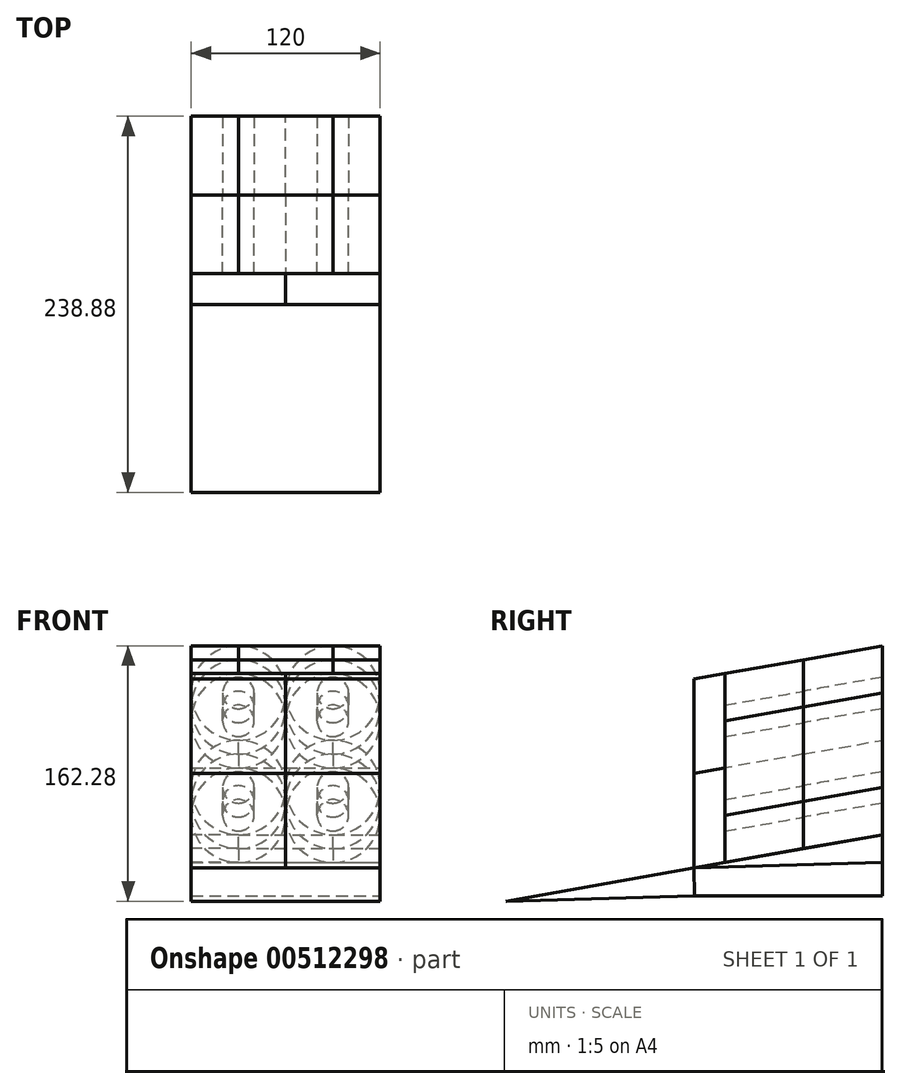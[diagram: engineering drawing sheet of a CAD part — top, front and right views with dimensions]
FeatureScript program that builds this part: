
annotation { "Feature Type Name" : "Feature", "Feature Type Description" : "" }
export const myFeature = defineFeature(function(context is Context, id is Id, definition is map)
    precondition{}
    {
        {
            var Q0;
            Q0=qCreatedBy(makeId("Front.planeOp"),FACE);
            var sketch = newSketch(context, id + "F0", { "sketchPlane" : qUnion([Q0])});
            skLineSegment(sketch, "E0", {"start": v(0, 0) * mm, "end": v(-30, 0) * mm});
            skLineSegment(sketch, "E1", {"start": v(-30, 0) * mm, "end": v(0, 0) * mm});
            skLineSegment(sketch, "E2", {"start": v(0, 0) * mm, "end": v(30, 0) * mm});
            skCircle(sketch, "E3", {"center": v(-30, 0) * mm, "radius": 30 * mm});
            skCircle(sketch, "E4", {"center": v(30, 0) * mm, "radius": 30 * mm});
            skLineSegment(sketch, "E5", {"start": v(30, 0) * mm, "end": v(40, 0) * mm});
            skLineSegment(sketch, "E6", {"start": v(-30, 0) * mm, "end": v(-40, 0) * mm});
            skCircle(sketch, "E7", {"center": v(-30, 0) * mm, "radius": 10 * mm});
            skCircle(sketch, "E8", {"center": v(30, 0) * mm, "radius": 10 * mm});
            skLineSegment(sketch, "E9", {"start": v(-30, 0) * mm, "end": v(-30, 60) * mm});
            skLineSegment(sketch, "E10", {"start": v(30, 0) * mm, "end": v(30, 60) * mm});
            skCircle(sketch, "E11", {"center": v(-30, 60) * mm, "radius": 30 * mm});
            skCircle(sketch, "E12", {"center": v(30, 60) * mm, "radius": 30 * mm});
            skLineSegment(sketch, "E13", {"start": v(-30, 60) * mm, "end": v(-20, 60) * mm});
            skLineSegment(sketch, "E14", {"start": v(30, 60) * mm, "end": v(20, 60) * mm});
            skCircle(sketch, "E15", {"center": v(-30, 60) * mm, "radius": 10 * mm});
            skCircle(sketch, "E16", {"center": v(30, 60) * mm, "radius": 10 * mm});
            skPoint(sketch, "E17", {"position": v(0, 30) * mm});
            skLineSegment(sketch, "E18.bottom", {"start": v(0, 30) * mm, "end": v(-60, 30) * mm});
            skLineSegment(sketch, "E18.top", {"start": v(0, -30) * mm, "end": v(-60, -30) * mm});
            skLineSegment(sketch, "E18.left", {"start": v(0, 30) * mm, "end": v(0, -30) * mm});
            skLineSegment(sketch, "E18.right", {"start": v(-60, 30) * mm, "end": v(-60, -30) * mm});
            skLineSegment(sketch, "E19.top", {"start": v(0, 90) * mm, "end": v(-60, 90) * mm});
            skLineSegment(sketch, "E19.left", {"start": v(0, 30) * mm, "end": v(0, 90) * mm});
            skLineSegment(sketch, "E19.right", {"start": v(-60, 30) * mm, "end": v(-60, 90) * mm});
            skLineSegment(sketch, "E20.bottom", {"start": v(0, -30) * mm, "end": v(60, -30) * mm});
            skLineSegment(sketch, "E20.top", {"start": v(0, 30) * mm, "end": v(60, 30) * mm});
            skLineSegment(sketch, "E20.left", {"start": v(0, -30) * mm, "end": v(0, 30) * mm});
            skLineSegment(sketch, "E20.right", {"start": v(60, -30) * mm, "end": v(60, 30) * mm});
            skLineSegment(sketch, "E21.top", {"start": v(0, 90) * mm, "end": v(60, 90) * mm});
            skLineSegment(sketch, "E21.right", {"start": v(60, 30) * mm, "end": v(60, 90) * mm});
            skSolve(sketch);
        }
        {
            var Q0;
            Q0=qCreatedBy(makeId("Front.planeOp"),FACE);
            var sketch = newSketch(context, id + "F1", { "sketchPlane" : qUnion([Q0])});
            skPoint(sketch, "E22", {"position": v(-30, 60) * mm});
            skPoint(sketch, "E23", {"position": v(30, 60) * mm});
            skPoint(sketch, "E24", {"position": v(-30, 0) * mm});
            skPoint(sketch, "E25", {"position": v(30, 0) * mm});
            skCircle(sketch, "E26", {"center": v(-30, 60) * mm, "radius": 10 * mm});
            skCircle(sketch, "E27", {"center": v(30, 60) * mm, "radius": 10 * mm});
            skCircle(sketch, "E28", {"center": v(30, 0) * mm, "radius": 10 * mm});
            skCircle(sketch, "E29", {"center": v(-30, 0) * mm, "radius": 10 * mm});
            skSolve(sketch);
        }
        {
            var Q0;
            Q0=qCreatedBy(makeId("Right.planeOp"),FACE);
            var sketch = newSketch(context, id + "F2", { "sketchPlane" : qUnion([Q0])});
            skLineSegment(sketch, "E30", {"start": v(0, -30) * mm, "end": v(50, -30) * mm});
            skLineSegment(sketch, "E31", {"start": v(0, -30) * mm, "end": v(0, -38.83) * mm});
            skLineSegment(sketch, "E32", {"start": v(0, -38.83) * mm, "end": v(0, -30) * mm});
            skLineSegment(sketch, "E33", {"start": v(50, -30) * mm, "end": v(50, -21.17) * mm});
            skLineSegment(sketch, "E34", {"start": v(0, -38.83) * mm, "end": v(-50, -38.83) * mm});
            skLineSegment(sketch, "E35", {"start": v(-50, -38.83) * mm, "end": v(0, -30) * mm});
            skLineSegment(sketch, "E36", {"start": v(50, -21.17) * mm, "end": v(0, -30) * mm});
            skSolve(sketch);
        }
        {
            var Q0;
            Q0 = qSketchRegion(id + "F1", true);
            var Q1;
            Q1=sQuery(id+"F2.wireOp",EDGE,"E35");
            var Q2;
            Q2=sQuery(id+"F2.wireOp",EDGE,"my1mdeSe-ST6u-0EiF-3ExV-mTvrdPK5u88H");
            sweep(context, id + "F3", {"profiles" : qUnion([Q0]), "path" : qUnion([Q1, Q2])});
        }
        {
            var Q0;
            Q0 = qSketchRegion(id + "F1", true);
            var Q1;
            Q1=sQuery(id+"F2.wireOp",EDGE,"E36");
            sweep(context, id + "F4", {"profiles" : qUnion([Q0]), "path" : qUnion([Q1])});
        }
        {
            var Q0;
            {var subQ3=sQuery(id+"F0.wireOp",EDGE,"E11");var subQ5=sQuery(id+"F0.wireOp",EDGE,"E12");var subQ6=makeQuery(id+"F0.imprint","INTERSECT",VERTEX,{"derivedFrom":[subQ3,subQ5]});Q0=makeQuery(id+"F0.imprint","IMPRINT",FACE,{"disambiguationData":[TD([[makeQuery(id+"F0.imprint","IMPRINT",EDGE,{"disambiguationData":[TD([[subQ6,1.0]])],"derivedFrom":subQ3}),-1.0]])]});}
            var Q1;
            {var subQ0=sQuery(id+"F0.wireOp",EDGE,"E20.left");var subQ3=sQuery(id+"F0.wireOp",EDGE,"E18.bottom");var subQ5=makeQuery(id+"F0.imprint","INTERSECT",VERTEX,{"derivedFrom":[subQ3,subQ0,sQuery(id+"F0.wireOp",EDGE,"E20.top"),sQuery(id+"F0.wireOp",EDGE,"E19.left")]});Q1=makeQuery(id+"F0.imprint","IMPRINT",FACE,{"disambiguationData":[TD([[makeQuery(id+"F0.imprint","IMPRINT",EDGE,{"disambiguationData":[TD([[subQ5,-1.0]])],"derivedFrom":subQ3}),1.0]])]});}
            var Q2;
            {var subQ0=sQuery(id+"F0.wireOp",EDGE,"E20.left");var subQ3=sQuery(id+"F0.wireOp",EDGE,"E20.top");var subQ5=makeQuery(id+"F0.imprint","INTERSECT",VERTEX,{"derivedFrom":[sQuery(id+"F0.wireOp",EDGE,"E18.bottom"),subQ0,subQ3,sQuery(id+"F0.wireOp",EDGE,"E19.left")]});Q2=makeQuery(id+"F0.imprint","IMPRINT",FACE,{"disambiguationData":[TD([[makeQuery(id+"F0.imprint","IMPRINT",EDGE,{"disambiguationData":[TD([[subQ5,-1.0]])],"derivedFrom":subQ3}),-1.0]])]});}
            var Q3;
            {var subQ0=sQuery(id+"F0.wireOp",EDGE,"E19.left");var subQ1=sQuery(id+"F0.wireOp",EDGE,"E12");var subQ2=makeQuery(id+"F0.imprint","INTERSECT",VERTEX,{"derivedFrom":[sQuery(id+"F0.wireOp",EDGE,"E11"),subQ1,subQ0]});Q3=makeQuery(id+"F0.imprint","IMPRINT",FACE,{"disambiguationData":[TD([[makeQuery(id+"F0.imprint","IMPRINT",EDGE,{"disambiguationData":[TD([[subQ2,-1.0]])],"derivedFrom":subQ1}),-1.0]])]});}
            var Q4;
            {var subQ0=sQuery(id+"F0.wireOp",EDGE,"E21.right");var subQ1=sQuery(id+"F0.wireOp",EDGE,"E12");var subQ2=makeQuery(id+"F0.imprint","INTERSECT",VERTEX,{"derivedFrom":[subQ1,subQ0]});Q4=makeQuery(id+"F0.imprint","IMPRINT",FACE,{"disambiguationData":[TD([[makeQuery(id+"F0.imprint","IMPRINT",EDGE,{"disambiguationData":[TD([[subQ2,1.0]])],"derivedFrom":subQ0}),1.0]])]});}
            var Q5;
            {var subQ0=sQuery(id+"F0.wireOp",EDGE,"E20.right");var subQ1=sQuery(id+"F0.wireOp",EDGE,"E4");var subQ2=makeQuery(id+"F0.imprint","INTERSECT",VERTEX,{"derivedFrom":[subQ1,subQ0]});Q5=makeQuery(id+"F0.imprint","IMPRINT",FACE,{"disambiguationData":[TD([[makeQuery(id+"F0.imprint","IMPRINT",EDGE,{"disambiguationData":[TD([[subQ2,-1.0]])],"derivedFrom":subQ0}),1.0]])]});}
            var Q6;
            {var subQ0=sQuery(id+"F0.wireOp",EDGE,"E20.right");var subQ1=sQuery(id+"F0.wireOp",EDGE,"E4");var subQ2=makeQuery(id+"F0.imprint","INTERSECT",VERTEX,{"derivedFrom":[subQ1,subQ0]});Q6=makeQuery(id+"F0.imprint","IMPRINT",FACE,{"disambiguationData":[TD([[makeQuery(id+"F0.imprint","IMPRINT",EDGE,{"disambiguationData":[TD([[subQ2,1.0]])],"derivedFrom":subQ1}),-1.0]])]});}
            var Q7;
            {var subQ1=sQuery(id+"F0.wireOp",EDGE,"E4");var subQ3=sQuery(id+"F0.wireOp",EDGE,"E20.bottom");var subQ4=makeQuery(id+"F0.imprint","INTERSECT",VERTEX,{"derivedFrom":[subQ1,subQ3]});Q7=makeQuery(id+"F0.imprint","IMPRINT",FACE,{"disambiguationData":[TD([[makeQuery(id+"F0.imprint","IMPRINT",EDGE,{"disambiguationData":[TD([[subQ4,1.0]])],"derivedFrom":subQ3}),1.0]])]});}
            var Q8;
            {var subQ1=sQuery(id+"F0.wireOp",EDGE,"E3");var subQ3=sQuery(id+"F0.wireOp",EDGE,"E18.top");var subQ4=makeQuery(id+"F0.imprint","INTERSECT",VERTEX,{"derivedFrom":[subQ1,subQ3]});Q8=makeQuery(id+"F0.imprint","IMPRINT",FACE,{"disambiguationData":[TD([[makeQuery(id+"F0.imprint","IMPRINT",EDGE,{"disambiguationData":[TD([[subQ4,1.0]])],"derivedFrom":subQ3}),-1.0]])]});}
            var Q9;
            {var subQ0=sQuery(id+"F0.wireOp",EDGE,"E18.right");var subQ1=sQuery(id+"F0.wireOp",EDGE,"E3");var subQ2=makeQuery(id+"F0.imprint","INTERSECT",VERTEX,{"derivedFrom":[subQ1,subQ0]});Q9=makeQuery(id+"F0.imprint","IMPRINT",FACE,{"disambiguationData":[TD([[makeQuery(id+"F0.imprint","IMPRINT",EDGE,{"disambiguationData":[TD([[subQ2,-1.0]])],"derivedFrom":subQ1}),-1.0]])]});}
            var Q10;
            {var subQ0=sQuery(id+"F0.wireOp",EDGE,"E18.right");var subQ1=sQuery(id+"F0.wireOp",EDGE,"E3");var subQ2=makeQuery(id+"F0.imprint","INTERSECT",VERTEX,{"derivedFrom":[subQ1,subQ0]});Q10=makeQuery(id+"F0.imprint","IMPRINT",FACE,{"disambiguationData":[TD([[makeQuery(id+"F0.imprint","IMPRINT",EDGE,{"disambiguationData":[TD([[subQ2,1.0]])],"derivedFrom":subQ0}),1.0]])]});}
            var Q11;
            {var subQ0=sQuery(id+"F0.wireOp",EDGE,"E19.right");var subQ1=sQuery(id+"F0.wireOp",EDGE,"E11");var subQ2=makeQuery(id+"F0.imprint","INTERSECT",VERTEX,{"derivedFrom":[subQ1,subQ0]});Q11=makeQuery(id+"F0.imprint","IMPRINT",FACE,{"disambiguationData":[TD([[makeQuery(id+"F0.imprint","IMPRINT",EDGE,{"disambiguationData":[TD([[subQ2,1.0]])],"derivedFrom":subQ0}),-1.0]])]});}
            var Q12;
            {var subQ0=sQuery(id+"F0.wireOp",EDGE,"E19.top");var subQ1=sQuery(id+"F0.wireOp",EDGE,"E11");var subQ2=makeQuery(id+"F0.imprint","INTERSECT",VERTEX,{"derivedFrom":[subQ1,subQ0]});Q12=makeQuery(id+"F0.imprint","IMPRINT",FACE,{"disambiguationData":[TD([[makeQuery(id+"F0.imprint","IMPRINT",EDGE,{"disambiguationData":[TD([[subQ2,-1.0]])],"derivedFrom":subQ1}),-1.0]])]});}
            var Q13;
            {var subQ0=sQuery(id+"F0.wireOp",EDGE,"E19.top");var subQ1=sQuery(id+"F0.wireOp",EDGE,"E11");var subQ2=makeQuery(id+"F0.imprint","INTERSECT",VERTEX,{"derivedFrom":[subQ1,subQ0]});Q13=makeQuery(id+"F0.imprint","IMPRINT",FACE,{"disambiguationData":[TD([[makeQuery(id+"F0.imprint","IMPRINT",EDGE,{"disambiguationData":[TD([[subQ2,1.0]])],"derivedFrom":subQ1}),-1.0]])]});}
            var Q14;
            {var subQ0=sQuery(id+"F0.wireOp",EDGE,"E21.top");var subQ1=sQuery(id+"F0.wireOp",EDGE,"E12");var subQ2=makeQuery(id+"F0.imprint","INTERSECT",VERTEX,{"derivedFrom":[subQ1,subQ0]});Q14=makeQuery(id+"F0.imprint","IMPRINT",FACE,{"disambiguationData":[TD([[makeQuery(id+"F0.imprint","IMPRINT",EDGE,{"disambiguationData":[TD([[subQ2,-1.0]])],"derivedFrom":subQ1}),-1.0]])]});}
            var Q15;
            {var subQ0=sQuery(id+"F0.wireOp",EDGE,"E21.top");var subQ1=sQuery(id+"F0.wireOp",EDGE,"E12");var subQ2=makeQuery(id+"F0.imprint","INTERSECT",VERTEX,{"derivedFrom":[subQ1,subQ0]});Q15=makeQuery(id+"F0.imprint","IMPRINT",FACE,{"disambiguationData":[TD([[makeQuery(id+"F0.imprint","IMPRINT",EDGE,{"disambiguationData":[TD([[subQ2,1.0]])],"derivedFrom":subQ1}),-1.0]])]});}
            var Q16;
            Q16=sQuery(id+"F2.wireOp",EDGE,"E36");
            sweep(context, id + "F5", {"profiles" : qUnion([Q0, Q1, Q2, Q3, Q4, Q5, Q6, Q7, Q8, Q9, Q10, Q11, Q12, Q13, Q14, Q15]), "path" : qUnion([Q16])});
        }
        {
            var Q0;
            {var subQ3=sQuery(id+"F0.wireOp",EDGE,"E11");var subQ5=sQuery(id+"F0.wireOp",EDGE,"E12");var subQ6=makeQuery(id+"F0.imprint","INTERSECT",VERTEX,{"derivedFrom":[subQ3,subQ5]});Q0=makeQuery(id+"F0.imprint","IMPRINT",FACE,{"disambiguationData":[TD([[makeQuery(id+"F0.imprint","IMPRINT",EDGE,{"disambiguationData":[TD([[subQ6,1.0]])],"derivedFrom":subQ3}),-1.0]])]});}
            var Q1;
            {var subQ0=sQuery(id+"F0.wireOp",EDGE,"E19.left");var subQ1=sQuery(id+"F0.wireOp",EDGE,"E12");var subQ2=makeQuery(id+"F0.imprint","INTERSECT",VERTEX,{"derivedFrom":[sQuery(id+"F0.wireOp",EDGE,"E11"),subQ1,subQ0]});Q1=makeQuery(id+"F0.imprint","IMPRINT",FACE,{"disambiguationData":[TD([[makeQuery(id+"F0.imprint","IMPRINT",EDGE,{"disambiguationData":[TD([[subQ2,-1.0]])],"derivedFrom":subQ1}),-1.0]])]});}
            var Q2;
            {var subQ0=sQuery(id+"F0.wireOp",EDGE,"E20.left");var subQ3=sQuery(id+"F0.wireOp",EDGE,"E20.top");var subQ5=makeQuery(id+"F0.imprint","INTERSECT",VERTEX,{"derivedFrom":[sQuery(id+"F0.wireOp",EDGE,"E18.bottom"),subQ0,subQ3,sQuery(id+"F0.wireOp",EDGE,"E19.left")]});Q2=makeQuery(id+"F0.imprint","IMPRINT",FACE,{"disambiguationData":[TD([[makeQuery(id+"F0.imprint","IMPRINT",EDGE,{"disambiguationData":[TD([[subQ5,-1.0]])],"derivedFrom":subQ3}),-1.0]])]});}
            var Q3;
            {var subQ0=sQuery(id+"F0.wireOp",EDGE,"E20.left");var subQ3=sQuery(id+"F0.wireOp",EDGE,"E18.bottom");var subQ5=makeQuery(id+"F0.imprint","INTERSECT",VERTEX,{"derivedFrom":[subQ3,subQ0,sQuery(id+"F0.wireOp",EDGE,"E20.top"),sQuery(id+"F0.wireOp",EDGE,"E19.left")]});Q3=makeQuery(id+"F0.imprint","IMPRINT",FACE,{"disambiguationData":[TD([[makeQuery(id+"F0.imprint","IMPRINT",EDGE,{"disambiguationData":[TD([[subQ5,-1.0]])],"derivedFrom":subQ3}),1.0]])]});}
            var Q4;
            {var subQ0=sQuery(id+"F0.wireOp",EDGE,"E21.top");var subQ1=sQuery(id+"F0.wireOp",EDGE,"E12");var subQ2=makeQuery(id+"F0.imprint","INTERSECT",VERTEX,{"derivedFrom":[subQ1,subQ0]});Q4=makeQuery(id+"F0.imprint","IMPRINT",FACE,{"disambiguationData":[TD([[makeQuery(id+"F0.imprint","IMPRINT",EDGE,{"disambiguationData":[TD([[subQ2,-1.0]])],"derivedFrom":subQ1}),-1.0]])]});}
            var Q5;
            {var subQ0=sQuery(id+"F0.wireOp",EDGE,"E19.top");var subQ1=sQuery(id+"F0.wireOp",EDGE,"E11");var subQ2=makeQuery(id+"F0.imprint","INTERSECT",VERTEX,{"derivedFrom":[subQ1,subQ0]});Q5=makeQuery(id+"F0.imprint","IMPRINT",FACE,{"disambiguationData":[TD([[makeQuery(id+"F0.imprint","IMPRINT",EDGE,{"disambiguationData":[TD([[subQ2,1.0]])],"derivedFrom":subQ1}),-1.0]])]});}
            var Q6;
            {var subQ0=sQuery(id+"F0.wireOp",EDGE,"E21.top");var subQ1=sQuery(id+"F0.wireOp",EDGE,"E12");var subQ2=makeQuery(id+"F0.imprint","INTERSECT",VERTEX,{"derivedFrom":[subQ1,subQ0]});Q6=makeQuery(id+"F0.imprint","IMPRINT",FACE,{"disambiguationData":[TD([[makeQuery(id+"F0.imprint","IMPRINT",EDGE,{"disambiguationData":[TD([[subQ2,1.0]])],"derivedFrom":subQ1}),-1.0]])]});}
            var Q7;
            {var subQ0=sQuery(id+"F0.wireOp",EDGE,"E21.right");var subQ1=sQuery(id+"F0.wireOp",EDGE,"E12");var subQ2=makeQuery(id+"F0.imprint","INTERSECT",VERTEX,{"derivedFrom":[subQ1,subQ0]});Q7=makeQuery(id+"F0.imprint","IMPRINT",FACE,{"disambiguationData":[TD([[makeQuery(id+"F0.imprint","IMPRINT",EDGE,{"disambiguationData":[TD([[subQ2,1.0]])],"derivedFrom":subQ0}),1.0]])]});}
            var Q8;
            {var subQ0=sQuery(id+"F0.wireOp",EDGE,"E20.right");var subQ1=sQuery(id+"F0.wireOp",EDGE,"E4");var subQ2=makeQuery(id+"F0.imprint","INTERSECT",VERTEX,{"derivedFrom":[subQ1,subQ0]});Q8=makeQuery(id+"F0.imprint","IMPRINT",FACE,{"disambiguationData":[TD([[makeQuery(id+"F0.imprint","IMPRINT",EDGE,{"disambiguationData":[TD([[subQ2,-1.0]])],"derivedFrom":subQ0}),1.0]])]});}
            var Q9;
            {var subQ0=sQuery(id+"F0.wireOp",EDGE,"E20.right");var subQ1=sQuery(id+"F0.wireOp",EDGE,"E4");var subQ2=makeQuery(id+"F0.imprint","INTERSECT",VERTEX,{"derivedFrom":[subQ1,subQ0]});Q9=makeQuery(id+"F0.imprint","IMPRINT",FACE,{"disambiguationData":[TD([[makeQuery(id+"F0.imprint","IMPRINT",EDGE,{"disambiguationData":[TD([[subQ2,1.0]])],"derivedFrom":subQ1}),-1.0]])]});}
            var Q10;
            {var subQ1=sQuery(id+"F0.wireOp",EDGE,"E4");var subQ3=sQuery(id+"F0.wireOp",EDGE,"E20.bottom");var subQ4=makeQuery(id+"F0.imprint","INTERSECT",VERTEX,{"derivedFrom":[subQ1,subQ3]});Q10=makeQuery(id+"F0.imprint","IMPRINT",FACE,{"disambiguationData":[TD([[makeQuery(id+"F0.imprint","IMPRINT",EDGE,{"disambiguationData":[TD([[subQ4,1.0]])],"derivedFrom":subQ3}),1.0]])]});}
            var Q11;
            {var subQ1=sQuery(id+"F0.wireOp",EDGE,"E3");var subQ3=sQuery(id+"F0.wireOp",EDGE,"E18.top");var subQ4=makeQuery(id+"F0.imprint","INTERSECT",VERTEX,{"derivedFrom":[subQ1,subQ3]});Q11=makeQuery(id+"F0.imprint","IMPRINT",FACE,{"disambiguationData":[TD([[makeQuery(id+"F0.imprint","IMPRINT",EDGE,{"disambiguationData":[TD([[subQ4,1.0]])],"derivedFrom":subQ3}),-1.0]])]});}
            var Q12;
            {var subQ0=sQuery(id+"F0.wireOp",EDGE,"E18.right");var subQ1=sQuery(id+"F0.wireOp",EDGE,"E3");var subQ2=makeQuery(id+"F0.imprint","INTERSECT",VERTEX,{"derivedFrom":[subQ1,subQ0]});Q12=makeQuery(id+"F0.imprint","IMPRINT",FACE,{"disambiguationData":[TD([[makeQuery(id+"F0.imprint","IMPRINT",EDGE,{"disambiguationData":[TD([[subQ2,1.0]])],"derivedFrom":subQ0}),1.0]])]});}
            var Q13;
            {var subQ0=sQuery(id+"F0.wireOp",EDGE,"E19.right");var subQ1=sQuery(id+"F0.wireOp",EDGE,"E11");var subQ2=makeQuery(id+"F0.imprint","INTERSECT",VERTEX,{"derivedFrom":[subQ1,subQ0]});Q13=makeQuery(id+"F0.imprint","IMPRINT",FACE,{"disambiguationData":[TD([[makeQuery(id+"F0.imprint","IMPRINT",EDGE,{"disambiguationData":[TD([[subQ2,1.0]])],"derivedFrom":subQ0}),-1.0]])]});}
            var Q14;
            {var subQ0=sQuery(id+"F0.wireOp",EDGE,"E19.top");var subQ1=sQuery(id+"F0.wireOp",EDGE,"E11");var subQ2=makeQuery(id+"F0.imprint","INTERSECT",VERTEX,{"derivedFrom":[subQ1,subQ0]});Q14=makeQuery(id+"F0.imprint","IMPRINT",FACE,{"disambiguationData":[TD([[makeQuery(id+"F0.imprint","IMPRINT",EDGE,{"disambiguationData":[TD([[subQ2,-1.0]])],"derivedFrom":subQ1}),-1.0]])]});}
            var Q15;
            {var subQ0=sQuery(id+"F0.wireOp",EDGE,"E18.right");var subQ1=sQuery(id+"F0.wireOp",EDGE,"E3");var subQ2=makeQuery(id+"F0.imprint","INTERSECT",VERTEX,{"derivedFrom":[subQ1,subQ0]});Q15=makeQuery(id+"F0.imprint","IMPRINT",FACE,{"disambiguationData":[TD([[makeQuery(id+"F0.imprint","IMPRINT",EDGE,{"disambiguationData":[TD([[subQ2,-1.0]])],"derivedFrom":subQ1}),-1.0]])]});}
            var Q16;
            Q16=sQuery(id+"F2.wireOp",EDGE,"E35");
            sweep(context, id + "F6", {"profiles" : qUnion([Q0, Q1, Q2, Q3, Q4, Q5, Q6, Q7, Q8, Q9, Q10, Q11, Q12, Q13, Q14, Q15]), "path" : qUnion([Q16])});
        }
        {
            var Q0;
            Q0=makeQuery(id+"F3.opSweep","CAP_FACE",FACE,{"disambiguationData":[OSD([sQuery(id+"F1.wireOp",EDGE,"E27"),sQuery(id+"F2.wireOp",VERTEX,"my1mdeSe-ST6u-0EiF-3ExV-mTvrdPK5u88H.end")])],"isStart":false});
            var sketch = newSketch(context, id + "F7", { "sketchPlane" : qUnion([Q0])});
            skLineSegment(sketch, "E37.bottom", {"start": v(60, 81.17) * mm, "end": v(0, 81.17) * mm});
            skLineSegment(sketch, "E37.top", {"start": v(60, 21.17) * mm, "end": v(0, 21.17) * mm});
            skLineSegment(sketch, "E37.left", {"start": v(60, 81.17) * mm, "end": v(60, 21.17) * mm});
            skLineSegment(sketch, "E37.right", {"start": v(0, 81.17) * mm, "end": v(0, 21.17) * mm});
            skSolve(sketch);
        }
        {
            var Q0;
            Q0=makeQuery(id+"F3.opSweep","CAP_FACE",FACE,{"disambiguationData":[OSD([sQuery(id+"F1.wireOp",EDGE,"E26"),sQuery(id+"F2.wireOp",VERTEX,"E35.start")])],"isStart":false});
            var sketch = newSketch(context, id + "F8", { "sketchPlane" : qUnion([Q0])});
            skPoint(sketch, "E38", {"position": v(-60, 81.17) * mm});
            skPoint(sketch, "E39", {"position": v(0, 81.17) * mm});
            skPoint(sketch, "E40", {"position": v(-60, 21.17) * mm});
            skLineSegment(sketch, "E41.bottom", {"start": v(0, 81.17) * mm, "end": v(-60, 81.17) * mm});
            skLineSegment(sketch, "E41.top", {"start": v(0, 21.17) * mm, "end": v(-60, 21.17) * mm});
            skLineSegment(sketch, "E41.left", {"start": v(0, 81.17) * mm, "end": v(0, 21.17) * mm});
            skLineSegment(sketch, "E41.right", {"start": v(-60, 81.17) * mm, "end": v(-60, 21.17) * mm});
            skPoint(sketch, "E42", {"position": v(-30, 51.17) * mm});
            skCircle(sketch, "E43", {"center": v(-30, 51.17) * mm, "radius": 10 * mm});
            skSolve(sketch);
        }
        {
            var Q0;
            Q0=makeQuery(id+"F3.opSweep","CAP_FACE",FACE,{"disambiguationData":[OSD([sQuery(id+"F1.wireOp",EDGE,"E28"),sQuery(id+"F2.wireOp",VERTEX,"E35.start")])],"isStart":false});
            var sketch = newSketch(context, id + "F9", { "sketchPlane" : qUnion([Q0])});
            skPoint(sketch, "E44", {"position": v(0, -38.83) * mm});
            skPoint(sketch, "E45", {"position": v(60, 21.17) * mm});
            skPoint(sketch, "E46", {"position": v(60, -38.83) * mm});
            skLineSegment(sketch, "E47.bottom", {"start": v(0, -38.83) * mm, "end": v(60, -38.83) * mm});
            skLineSegment(sketch, "E47.top", {"start": v(0, 21.17) * mm, "end": v(60, 21.17) * mm});
            skLineSegment(sketch, "E47.left", {"start": v(0, -38.83) * mm, "end": v(0, 21.17) * mm});
            skLineSegment(sketch, "E47.right", {"start": v(60, -38.83) * mm, "end": v(60, 21.17) * mm});
            skSolve(sketch);
        }
        {
            var Q0;
            Q0=qCreatedBy(makeId("Right.planeOp"),FACE);
            var sketch = newSketch(context, id + "F10", { "sketchPlane" : qUnion([Q0])});
            skPoint(sketch, "E48", {"position": v(-50, -8.83) * mm});
            skLineSegment(sketch, "E49", {"start": v(-50, -8.83) * mm, "end": v(-69.7, -12.31) * mm});
            skPoint(sketch, "E50", {"position": v(-50, 51.17) * mm});
            skLineSegment(sketch, "E51", {"start": v(-50, 51.17) * mm, "end": v(-69.7, 47.69) * mm});
            skSolve(sketch);
        }
        {
            var Q0;
            Q0=makeQuery(id+"F7.imprint","IMPRINT",FACE,{"disambiguationData":[TD([[makeQuery(id+"F7.imprint","IMPRINT",EDGE,{"derivedFrom":sQuery(id+"F7.wireOp",EDGE,"E37.bottom")}),1.0]])]});
            var Q1;
            Q1=makeQuery(id+"F7.imprint","IMPRINT",FACE,{"disambiguationData":[TD([[makeQuery(id+"F7.imprint","IMPRINT",EDGE,{"derivedFrom":makeQuery(id+"F3.opSweep","CAP_EDGE",EDGE,{"disambiguationData":[OSD([sQuery(id+"F1.wireOp",EDGE,"E27"),sQuery(id+"F2.wireOp",VERTEX,"my1mdeSe-ST6u-0EiF-3ExV-mTvrdPK5u88H.end")])],"isStart":false})}),1.0]])]});
            var Q2;
            Q2=sQuery(id+"F10.wireOp",EDGE,"E51");
            sweep(context, id + "F11", {"profiles" : qUnion([Q0, Q1]), "path" : qUnion([Q2])});
        }
        {
            var Q0;
            Q0 = qSketchRegion(id + "F8", true);
            var Q1;
            Q1=makeQuery(id+"F8.imprint","IMPRINT",FACE,{"disambiguationData":[TD([[makeQuery(id+"F8.imprint","IMPRINT",EDGE,{"derivedFrom":sQuery(id+"F8.wireOp",EDGE,"E43")}),1.0]])]});
            var Q2;
            Q2=sQuery(id+"F10.wireOp",EDGE,"E51");
            sweep(context, id + "F12", {"profiles" : qUnion([Q0, Q1]), "path" : qUnion([Q2])});
        }
        {
            var Q0;
            Q0 = qSketchRegion(id + "F9", true);
            var Q1;
            Q1=sQuery(id+"F10.wireOp",EDGE,"E49");
            sweep(context, id + "F13", {"profiles" : qUnion([Q0]), "path" : qUnion([Q1])});
        }
        {
            var Q0;
            Q0=makeQuery(id+"F3.opSweep","CAP_FACE",FACE,{"disambiguationData":[OSD([sQuery(id+"F1.wireOp",EDGE,"E29"),sQuery(id+"F2.wireOp",VERTEX,"E35.start")])],"isStart":false});
            var sketch = newSketch(context, id + "F14", { "sketchPlane" : qUnion([Q0])});
            skPoint(sketch, "E52", {"position": v(-60, 21.17) * mm});
            skPoint(sketch, "E53", {"position": v(0, 21.17) * mm});
            skPoint(sketch, "E54", {"position": v(-60, -38.83) * mm});
            skLineSegment(sketch, "E55.bottom", {"start": v(-60, -38.83) * mm, "end": v(0, -38.83) * mm});
            skLineSegment(sketch, "E55.top", {"start": v(-60, 21.17) * mm, "end": v(0, 21.17) * mm});
            skLineSegment(sketch, "E55.left", {"start": v(-60, -38.83) * mm, "end": v(-60, 21.17) * mm});
            skLineSegment(sketch, "E55.right", {"start": v(0, -38.83) * mm, "end": v(0, 21.17) * mm});
            skSolve(sketch);
        }
        {
            var Q0;
            Q0 = qSketchRegion(id + "F14", true);
            var Q1;
            Q1=sQuery(id+"F10.wireOp",EDGE,"E49");
            sweep(context, id + "F15", {"profiles" : qUnion([Q0]), "path" : qUnion([Q1])});
        }
        {
            var Q0;
            Q0=makeQuery(id+"F6.opSweep","SWEPT_FACE",FACE,{"disambiguationData":[OSD([sQuery(id+"F0.wireOp",EDGE,"E20.right"),sQuery(id+"F2.wireOp",EDGE,"E35")])]});
            var sketch = newSketch(context, id + "F16", { "sketchPlane" : qUnion([Q0])});
            skPoint(sketch, "E56", {"position": v(-69.7, -42.31) * mm});
            skPoint(sketch, "E57", {"position": v(50, -21.17) * mm});
            skLineSegment(sketch, "E58", {"start": v(-69.7, -42.31) * mm, "end": v(50, -21.17) * mm});
            skLineSegment(sketch, "E59", {"start": v(50, -38.83) * mm, "end": v(-69.7, -42.31) * mm});
            skLineSegment(sketch, "E60", {"start": v(50, -38.83) * mm, "end": v(50, -21.17) * mm});
            skSolve(sketch);
        }
        {
            var Q0;
            {var subQ0=sQuery(id+"F16.wireOp",EDGE,"E59");Q0=makeQuery(id+"F16.imprint","IMPRINT",FACE,{"disambiguationData":[TD([[makeQuery(id+"F16.imprint","IMPRINT",EDGE,{"derivedFrom":subQ0}),-1.0]])]});}
            extrude(context, id + "F17", {"entities" : qUnion([Q0]), "oppositeDirection" : true, "depth" : 120 * mm});
        }
        {
            var Q0;
            Q0=makeQuery(id+"F17.opExtrude","CAP_FACE",FACE,{"disambiguationData":[OSD([sQuery(id+"F16.wireOp",EDGE,"E58"),sQuery(id+"F16.wireOp",EDGE,"E59"),sQuery(id+"F16.wireOp",EDGE,"E60")])],"isStart":true});
            var sketch = newSketch(context, id + "F18", { "sketchPlane" : qUnion([Q0])});
            skPoint(sketch, "E61", {"position": v(-69.7, -42.31) * mm});
            skLineSegment(sketch, "E62", {"start": v(-69.7, -42.31) * mm, "end": v(-69.18, -59.97) * mm});
            skLineSegment(sketch, "E63", {"start": v(-69.18, -59.97) * mm, "end": v(-188.88, -63.45) * mm});
            skLineSegment(sketch, "E64", {"start": v(-188.88, -63.45) * mm, "end": v(-69.7, -42.31) * mm});
            skSolve(sketch);
        }
        {
            var Q0;
            Q0 = qSketchRegion(id + "F18", true);
            extrude(context, id + "F19", {"entities" : qUnion([Q0]), "oppositeDirection" : true, "depth" : 120 * mm});
        }
        {
            var Q0;
            Q0=makeQuery(id+"F19.opExtrude","CAP_FACE",FACE,{"disambiguationData":[OSD([sQuery(id+"F18.wireOp",EDGE,"E62"),sQuery(id+"F18.wireOp",EDGE,"E63"),sQuery(id+"F18.wireOp",EDGE,"E64")])],"isStart":true});
            var sketch = newSketch(context, id + "F20", { "sketchPlane" : qUnion([Q0])});
            skPoint(sketch, "E65", {"position": v(-69.7, -42.31) * mm});
            skPoint(sketch, "E66", {"position": v(-69.18, -59.97) * mm});
            skPoint(sketch, "E67", {"position": v(50, -38.83) * mm});
            skPoint(sketch, "E68", {"position": v(50, -59.97) * mm});
            skLineSegment(sketch, "E69", {"start": v(-69.18, -59.97) * mm, "end": v(50, -59.97) * mm});
            skLineSegment(sketch, "E70", {"start": v(50, -59.97) * mm, "end": v(50, -38.83) * mm});
            skLineSegment(sketch, "E71", {"start": v(-69.7, -42.31) * mm, "end": v(-69.18, -59.97) * mm});
            skLineSegment(sketch, "E72", {"start": v(-69.7, -42.31) * mm, "end": v(50, -38.83) * mm});
            skSolve(sketch);
        }
        {
            var Q0;
            Q0=makeQuery(id+"F20.imprint","IMPRINT",FACE,{"disambiguationData":[TD([[makeQuery(id+"F20.imprint","IMPRINT",EDGE,{"derivedFrom":sQuery(id+"F20.wireOp",EDGE,"E69")}),1.0]])]});
            extrude(context, id + "F21", {"entities" : qUnion([Q0]), "oppositeDirection" : true, "depth" : 120 * mm});
        }
    });
